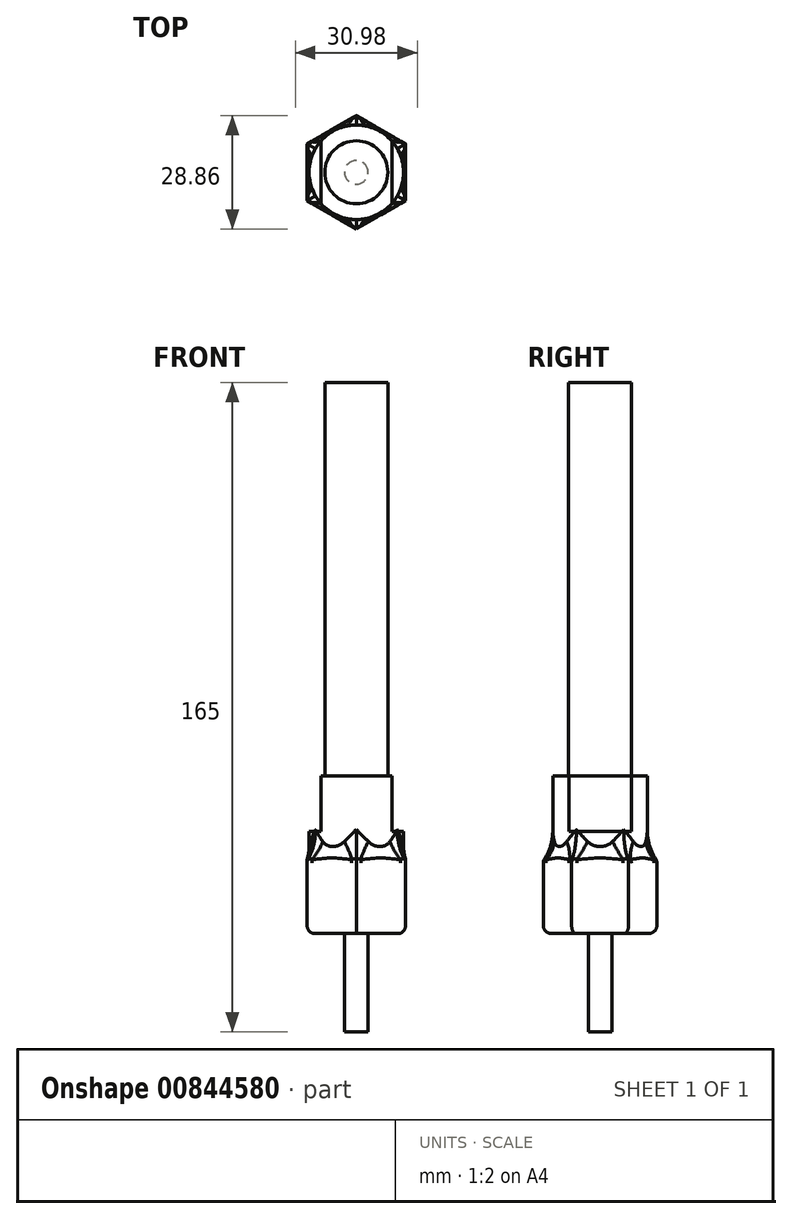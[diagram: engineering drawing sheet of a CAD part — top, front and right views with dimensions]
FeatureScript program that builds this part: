
annotation { "Feature Type Name" : "Feature", "Feature Type Description" : "" }
export const myFeature = defineFeature(function(context is Context, id is Id, definition is map)
    precondition{}
    {
        {
            var Q0;
            Q0=qCreatedBy(makeId("Top.planeOp"),FACE);
            var sketch = newSketch(context, id + "F0", { "sketchPlane" : qUnion([Q0])});
            skCircle(sketch, "E0", {"center": v(0, 0) * mm, "radius": 12 * mm});
            skSolve(sketch);
        }
        {
            var Q0;
            Q0=makeQuery(id+"F0.imprint","IMPRINT",FACE,{"disambiguationData":[TD([[makeQuery(id+"F0.imprint","IMPRINT",EDGE,{"derivedFrom":sQuery(id+"F0.wireOp",EDGE,"E0")}),1.0]])]});
            extrude(context, id + "F1", {"entities" : qUnion([Q0]), "depth" : 20 * mm, "offsetDistance" : 25 * mm});
        }
        {
            var Q0;
            Q0=makeQuery(id+"F1.opExtrude","CAP_FACE",FACE,{"disambiguationData":[OSD([sQuery(id+"F0.wireOp",EDGE,"E0")])],"isStart":true});
            var sketch = newSketch(context, id + "F2", { "sketchPlane" : qUnion([Q0])});
            skCircle(sketch, "E1.cCircle", {"center": v(0, 0) * mm, "radius": 12.5 * mm, "construction": true});
            skLineSegment(sketch, "E1.0", {"start": v(12.5, 7.22) * mm, "end": v(12.5, -7.22) * mm});
            skLineSegment(sketch, "E1.1", {"start": v(12.5, -7.22) * mm, "end": v(0, -14.43) * mm});
            skLineSegment(sketch, "E1.2", {"start": v(0, -14.43) * mm, "end": v(-12.5, -7.22) * mm});
            skLineSegment(sketch, "E1.3", {"start": v(-12.5, -7.22) * mm, "end": v(-12.5, 7.22) * mm});
            skLineSegment(sketch, "E1.4", {"start": v(-12.5, 7.22) * mm, "end": v(0, 14.43) * mm});
            skLineSegment(sketch, "E1.5", {"start": v(0, 14.43) * mm, "end": v(12.5, 7.22) * mm});
            skPoint(sketch, "E1.0.midPoint", {"position": v(12.5, 0) * mm});
            skSolve(sketch);
        }
        {
            var Q0;
            Q0=makeQuery(id+"F2.imprint","IMPRINT",FACE,{"disambiguationData":[TD([[makeQuery(id+"F2.imprint","IMPRINT",EDGE,{"derivedFrom":sQuery(id+"F2.wireOp",EDGE,"E1.0")}),-1.0]])]});
            var Q1;
            Q1=makeQuery(id+"F2.imprint","IMPRINT",FACE,{"disambiguationData":[TD([[makeQuery(id+"F2.imprint","IMPRINT",EDGE,{"derivedFrom":makeQuery(id+"F1.opExtrude","CAP_EDGE",EDGE,{"disambiguationData":[OSD([sQuery(id+"F0.wireOp",EDGE,"E0")])],"isStart":true})}),-1.0]])]});
            extrude(context, id + "F3", {"entities" : qUnion([Q0, Q1]), "operationType" : NewBodyOperationType.ADD, "depth" : 20 * mm, "offsetDistance" : 25 * mm});
        }
        {
            var Q0;
            Q0=makeQuery(id+"F3.opExtrude","CAP_EDGE",EDGE,{"disambiguationData":[OSD([sQuery(id+"F2.wireOp",EDGE,"E1.0")])],"isStart":true});
            var Q1;
            Q1=makeQuery(id+"F3.opExtrude","CAP_EDGE",EDGE,{"disambiguationData":[OSD([sQuery(id+"F2.wireOp",EDGE,"E1.1")])],"isStart":true});
            var Q2;
            Q2=makeQuery(id+"F3.opExtrude","CAP_EDGE",EDGE,{"disambiguationData":[OSD([sQuery(id+"F2.wireOp",EDGE,"E1.2")])],"isStart":true});
            var Q3;
            Q3=makeQuery(id+"F3.opExtrude","CAP_EDGE",EDGE,{"disambiguationData":[OSD([sQuery(id+"F2.wireOp",EDGE,"E1.3")])],"isStart":true});
            var Q4;
            Q4=makeQuery(id+"F3.opExtrude","CAP_EDGE",EDGE,{"disambiguationData":[OSD([sQuery(id+"F2.wireOp",EDGE,"E1.4")])],"isStart":true});
            var Q5;
            Q5=makeQuery(id+"F3.opExtrude","CAP_EDGE",EDGE,{"disambiguationData":[OSD([sQuery(id+"F2.wireOp",EDGE,"E1.5")])],"isStart":true});
            fillet(context, id + "F4", {"entities" : qUnion([Q0, Q1, Q2, Q3, Q4, Q5]), "radius" : 2 * mm, "tangentPropagation" : true, "allowEdgeOverflow" : false});
        }
        {
            var Q0;
            Q0=makeQuery(id+"F4.opFillet","BLEND_EDGE",EDGE,{"blendedFrom":[makeQuery(id+"F3.opExtrude","CAP_EDGE",EDGE,{"disambiguationData":[OSD([sQuery(id+"F2.wireOp",EDGE,"E1.4")])],"isStart":true}),makeQuery(id+"F1.opExtrude","SWEPT_FACE",FACE,{"disambiguationData":[OSD([sQuery(id+"F0.wireOp",EDGE,"E0")])]})],"blendedInto":[makeQuery(id+"F1.opExtrude","SWEPT_FACE",FACE,{"disambiguationData":[OSD([sQuery(id+"F0.wireOp",EDGE,"E0")])]})]});
            fillet(context, id + "F5", {"entities" : qUnion([Q0]), "radius" : 10 * mm, "tangentPropagation" : true, "allowEdgeOverflow" : false});
        }
        {
            var Q0;
            Q0=makeQuery(id+"F3.opExtrude","CAP_EDGE",EDGE,{"disambiguationData":[OSD([sQuery(id+"F2.wireOp",EDGE,"E1.0")])],"isStart":false});
            var Q1;
            Q1=makeQuery(id+"F3.opExtrude","CAP_EDGE",EDGE,{"disambiguationData":[OSD([sQuery(id+"F2.wireOp",EDGE,"E1.1")])],"isStart":false});
            var Q2;
            Q2=makeQuery(id+"F3.opExtrude","CAP_EDGE",EDGE,{"disambiguationData":[OSD([sQuery(id+"F2.wireOp",EDGE,"E1.2")])],"isStart":false});
            var Q3;
            Q3=makeQuery(id+"F3.opExtrude","CAP_EDGE",EDGE,{"disambiguationData":[OSD([sQuery(id+"F2.wireOp",EDGE,"E1.3")])],"isStart":false});
            var Q4;
            Q4=makeQuery(id+"F3.opExtrude","CAP_EDGE",EDGE,{"disambiguationData":[OSD([sQuery(id+"F2.wireOp",EDGE,"E1.4")])],"isStart":false});
            var Q5;
            Q5=makeQuery(id+"F3.opExtrude","CAP_EDGE",EDGE,{"disambiguationData":[OSD([sQuery(id+"F2.wireOp",EDGE,"E1.5")])],"isStart":false});
            fillet(context, id + "F6", {"entities" : qUnion([Q0, Q1, Q2, Q3, Q4, Q5]), "radius" : 2 * mm, "tangentPropagation" : true, "allowEdgeOverflow" : false});
        }
        {
            var Q0;
            Q0=makeQuery(id+"F1.opExtrude","CAP_FACE",FACE,{"disambiguationData":[OSD([sQuery(id+"F0.wireOp",EDGE,"E0")])],"isStart":false});
            var sketch = newSketch(context, id + "F7", { "sketchPlane" : qUnion([Q0])});
            skCircle(sketch, "E2", {"center": v(0, 0) * mm, "radius": 8 * mm});
            skSolve(sketch);
        }
        {
            var Q0;
            Q0=makeQuery(id+"F7.imprint","IMPRINT",FACE,{"disambiguationData":[TD([[makeQuery(id+"F7.imprint","IMPRINT",EDGE,{"derivedFrom":sQuery(id+"F7.wireOp",EDGE,"E2")}),1.0]])]});
            extrude(context, id + "F8", {"entities" : qUnion([Q0]), "operationType" : NewBodyOperationType.ADD, "depth" : 100 * mm, "offsetDistance" : 25 * mm});
        }
        {
            var Q0;
            Q0=makeQuery(id+"F3.opExtrude","CAP_FACE",FACE,{"disambiguationData":[OSD([sQuery(id+"F2.wireOp",EDGE,"E1.0"),sQuery(id+"F2.wireOp",EDGE,"E1.1"),sQuery(id+"F2.wireOp",EDGE,"E1.2"),sQuery(id+"F2.wireOp",EDGE,"E1.3"),sQuery(id+"F2.wireOp",EDGE,"E1.4"),sQuery(id+"F2.wireOp",EDGE,"E1.5")])],"isStart":false});
            var sketch = newSketch(context, id + "F9", { "sketchPlane" : qUnion([Q0])});
            skCircle(sketch, "E3", {"center": v(0, 0) * mm, "radius": 3 * mm});
            skSolve(sketch);
        }
        {
            var Q0;
            Q0=makeQuery(id+"F9.imprint","IMPRINT",FACE,{"disambiguationData":[TD([[makeQuery(id+"F9.imprint","IMPRINT",EDGE,{"derivedFrom":sQuery(id+"F9.wireOp",EDGE,"E3")}),1.0]])]});
            extrude(context, id + "F10", {"entities" : qUnion([Q0]), "operationType" : NewBodyOperationType.ADD, "depth" : 25 * mm, "offsetDistance" : 25 * mm});
        }
        {
            var Q0;
            Q0=makeQuery(id+"F1.opExtrude","CAP_FACE",FACE,{"disambiguationData":[OSD([sQuery(id+"F0.wireOp",EDGE,"E0")])],"isStart":false});
            var sketch = newSketch(context, id + "F11", { "sketchPlane" : qUnion([Q0])});
            skLineSegment(sketch, "E4.bottom", {"start": v(9, -17.44) * mm, "end": v(-9, -17.44) * mm});
            skLineSegment(sketch, "E4.top", {"start": v(9, 17.44) * mm, "end": v(-9, 17.44) * mm});
            skLineSegment(sketch, "E4.left", {"start": v(9, -17.44) * mm, "end": v(9, 17.44) * mm});
            skLineSegment(sketch, "E4.right", {"start": v(-9, -17.44) * mm, "end": v(-9, 17.44) * mm});
            skPoint(sketch, "E4.middle", {"position": v(0, 0) * mm});
            skSolve(sketch);
        }
        {
            var Q0;
            {var subQ0=sQuery(id+"F11.wireOp",EDGE,"E4.right");var subQ1=makeQuery(id+"F1.opExtrude","CAP_EDGE",EDGE,{"disambiguationData":[OSD([sQuery(id+"F0.wireOp",EDGE,"E0")])],"isStart":false});var subQ2=makeQuery(id+"F11.imprint","INTERSECT",VERTEX,{"disambiguationData":[OD(0.0)],"derivedFrom":[subQ1,subQ0]});Q0=makeQuery(id+"F11.imprint","IMPRINT",FACE,{"disambiguationData":[TD([[makeQuery(id+"F11.imprint","IMPRINT",EDGE,{"disambiguationData":[TD([[subQ2,-1.0]])],"derivedFrom":subQ0}),1.0]])]});}
            var Q1;
            {var subQ0=sQuery(id+"F11.wireOp",EDGE,"E4.left");var subQ1=makeQuery(id+"F1.opExtrude","CAP_EDGE",EDGE,{"disambiguationData":[OSD([sQuery(id+"F0.wireOp",EDGE,"E0")])],"isStart":false});var subQ2=makeQuery(id+"F11.imprint","INTERSECT",VERTEX,{"disambiguationData":[OD(0.0)],"derivedFrom":[subQ1,subQ0]});Q1=makeQuery(id+"F11.imprint","IMPRINT",FACE,{"disambiguationData":[TD([[makeQuery(id+"F11.imprint","IMPRINT",EDGE,{"disambiguationData":[TD([[subQ2,-1.0]])],"derivedFrom":subQ0}),-1.0]])]});}
            extrude(context, id + "F12", {"entities" : qUnion([Q0, Q1]), "operationType" : NewBodyOperationType.REMOVE, "oppositeDirection" : true, "depth" : 14 * mm, "offsetDistance" : 25 * mm});
        }
    });
